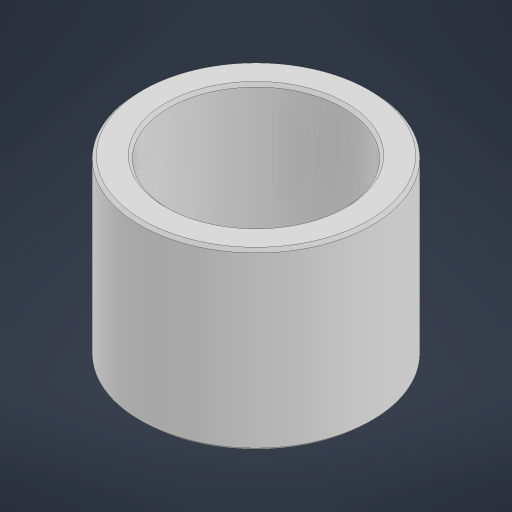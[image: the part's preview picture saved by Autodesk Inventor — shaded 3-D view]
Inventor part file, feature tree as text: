
AUTODESK INVENTOR PART (.ipt)
format: ipt  version: 2023 (Build 270158000, 158)  size: 171,520 bytes
history: native  units: in
note: dims shown in document units (in); Inventor stores cm internally (conversion verified against a paired STEP export)
features: chamfer x1
ambient origin geometry x8: Origin, YZ Plane, XZ Plane, XY Plane, X Axis, Y Axis, Z Axis, Center Point
bodies: Solid1 (feature_tree)
feature tree (1):
  chamfer  "Chamfer1"  [1 undecoded]
note: 1 required parameter value undecoded (feature->parameter linkage not recoverable at this tier; creation-order binding heuristic only, values carry confidence <= 0.55)
